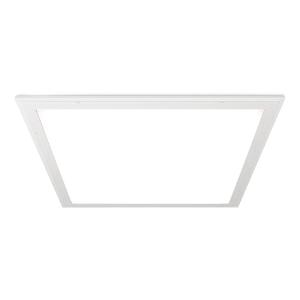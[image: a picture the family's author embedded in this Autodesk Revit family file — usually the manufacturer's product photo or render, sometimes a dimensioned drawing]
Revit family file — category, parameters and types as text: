
# Revit family: 3f_filippi_-_l_650_luce_diffusa_vss_3f_filippi_-_21894_-_l_650_75w-940_dali_vss_596x596
name_source: partatom
category: Lighting Fixtures
units: mm (PartAtom-declared; Revit-internal decimal feet)

## family parameters
Cut with Voids When Loaded = No
Host = Face
Light Source = No
Part Type = Normal
Room Calculation Point = No
Round Connector Dimension = Use Diameter
Shared = No

## types (1)
- 3F Filippi - L 650 Luce Diffusa VSS (1 x LED, 6830 lm, 81 W, 4000 K)
    Apparent Load = 81 VA
    Approval mark = ENEC
    CIE Flux Codes = 63 92 98 100 100
    Color Rendering = 90
    Color Temperature = 4000 K
    Control Gear = Electronic transformer
    Default Elevation = 1800 mm
    Description = ILLUMINOTECHNICAL
Luminous efficiency 100% (DLOR 100%, ULOR 0%).
Initial luminous flux of the luminaire 6830 lm.
Direct symmetric distribution.
Installation Interdistance Transv.D = 1.17 x hu - Long.D = 1.16 x hu.
Average luminance <3000 cd/m² for radial angles >65°.
Tabular UGR (CIE 117 - 4H-8H; S=0.25H; 70/50/20): RUG 19.2 - 19.1.
Beam angle: 90° - 88°.
Luminous efficacy 84 lm/W.
Lifetime (L93/B10): 30000 h. (tq+25°C)
Lifetime (L90/B10): 50000 h. (tq+25°C)
Lifetime (L85/B10): 80000 h. (tq+25°C)
Lifetime (L80/B10): 100000 h. (tq+25°C)
Sudden decreased luminous flux after 50000 hours: 0% (C0).
Photobiological safety in compliance with IEC/TR 62778: RG0 risk exempt, (IEC 62471).
In compliance with IEC/EN 62722-2-1 - IEC/EN 62717 standards.

SOURCE
Squared LED module 75W/940.
Source with special protection against aggressive chemically-volatile substances for standard LED technology.
Energy efficiency class (UE 2019/2020 - UE 2019/2015): E.
CIE 13.3 Colour rendering index: CRI >90 (R9 >50%).
IES TM-30 Fidelity Index: Rf = 92 Rg = 101.
CCT nominal colour temperature 4000 K.
Colour initial tolerance (MacAdam): SDCM 3.

MECHANICAL
Housing in galvannealed steel, painted in white epoxy-polyester.
Perimetral frame in white stainless steel.
VSS moulded laminated dipped glass, non-combustible, thickness 7 mm.
Anti-glare opal polycarbonate filter for brightness uniformity.
Luminaire with limited surface temperature. - D - (EN 60598-2-24)
Dimensions: 596x596 mm, height 90 mm. Weight 9.7 kg.
IP66 protection degree for exposed part, IP64 for recessed part.
Mechanical strength to impacts IK08 (5 joule).
Glow-wire test resistance 650°C.

ELECTRICAL
Halogen Free DALI-2 DATI (Parts 251, 252, 253), PUSH-DIM, electronic wiring 230V-50/60Hz, power factor 0.95 at full load, THD <25%, constant output current, SELV, class I, 1 driver, 1 DALI addresse.
Power of the luminaire 81 W.
CE - IEC 60598-1 - EN 60598-1.
SAFE FLICKER: PstLM=<1 and SVM=<0.4 (IEC TR 61547-1 and IEC TR 63158), to ensure a more comfortable and safe light.
Luminaire compliant with EN 60598-2-22 for power supply from a centralised emergency system CPSS (Central Power Supply System), not incorporated in the luminaire - high risk areas excluded. The default power and flux are 100% in AC and 15% in DC.
Ambient temperature from 0°C to +40°C.
Temperature class T6 max 85°C.
5-pole terminal block (L-N-PE-DA/DA) quick connection for line connection with connection capacity 2x2.5 mm² per poles.
Relative humidity UR: <85%.

INSTALLATION
Lay-in recessed fitting.
All accessories dedicated to this product are available on the Catalog and on our website www.3F-Filippi.com.

APPLICATIONS
Suitable product for food production plants (HACCP), IFS (Food Version 6), BRC (GSFS Food Version 7).
Environments: hospital premises, transit areas, laboratories, platform-roof, underpasses.
Environments: sterilized, aseptic.
In hospital environments, food industry or machines with parts in motion, with considerable sudden temperature changes, and in general in any environments requiring total protection against falling fragments, use luminaires with laminated glass only.
Tempered glass is not immune to falling fragments from harmless and caused by shocks or exceptionally derived from the tempering process.
Environments requiring a high level of protection and simplified cleaning.
Environments with exacting visual tasks, where diffused soft light for optimum visual comfort is required.

LIGHT MANAGEMENT
Recommended minimum setting: 10%.
The luminaire, equipped with (DALI-2 DATI) driver, can be controlled manually with 3F Easy Dim technology or automatically/manually with wired or wireless DALI/D2D control systems.
The D2D driver guarantees interoperability with other devices with the same certification by making the following information available:
Device Data (Part 251), Energy Report (Part 252), Diagnosis & Maintenance (Part 253).
In electrical systems without a regulation system (manual or automatic) and DALI bus, a suitable jumper must be made on the DA-DA terminals of the appliance.

WARNING
Luminaire designed for disposal/recycling at end-of-life.
Replaceable (LED only) light source by a professional. Replaceable control gear by a professional.
    Height = 0 mm  [stored 0 ft]
    Lamp = 1 x LED
    Lamp Light Flux = 6830 lm
    Lamp Power = 81 W
    Lamp count = 1
    Length = 596 mm
    Lifetime = 50000 h
    Luminous efficacy = 84 lm/W
    Manufacturer = 3F Filippi
    ModVariant = No
    Model = 3F Filippi - 21894 - L 650 75W-940 DALI VSS 596x596
    Mounting Place = Ceiling
    Mounting Type = Recessed
    Number of Poles = 1
    OnlyDefault = Yes
    Power Factor = 1
    Product Name = 3F Filippi - L 650 Luce Diffusa VSS
    Product group = recessed luminaire
    ProductGroupID = 4
    Protection Class = Protection class I
    Protection Degree = IP 64
    RLX_Detail_Level = 1
    RLX_Emergency_Light_Flux = 0 lm
    RLX_Emergency_Type = 0
    RLX_Emergency_Type_DB = No
    RlxData = <blob elided: 101017 chars, md5=d9501ce6>
    Socket = socket
    Standby Power = 0 W
    System Light Flux = 6830 lm
    System Power = 81 W
    Type Comments = Product without accessories
    Type Image = 3ffilippi_l_650_luce_diffusa_vss.jpg
    URL = http://relux.com
    VarID = ---
    Voltage = 0 V
    Weight = 0.00 kg
    Width = 596 mm

note: [stored X ft] marks values corroborated as IEEE doubles in the binary element streams (Revit-internal decimal feet)

## geometry (parser evidence)
native form markers: Blend x4, Sweep x10
no freeform markers — native parametric forms only
